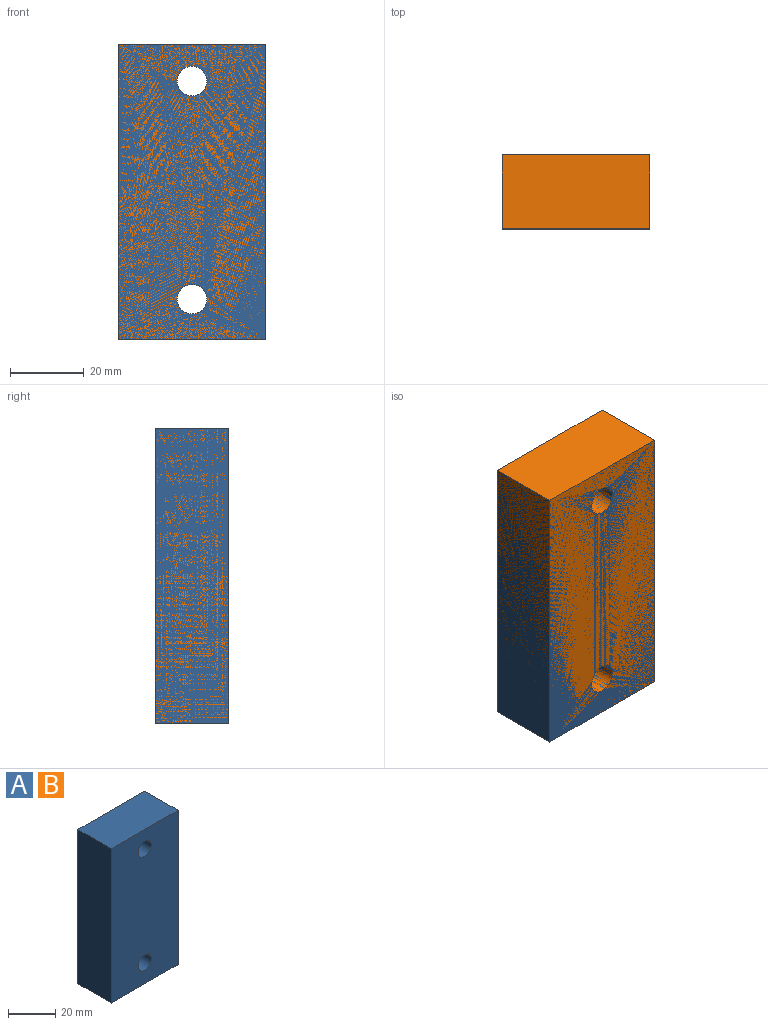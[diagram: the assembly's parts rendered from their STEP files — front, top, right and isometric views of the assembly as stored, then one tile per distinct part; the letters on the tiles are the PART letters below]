
ASSEMBLY  parts=2 mates=1
PART A: 8 faces, bbox 40x20x80 mm
  f0: plane 80x40mm, normal (0,-1,0), area 3099.5mm2, adj f1,f3,f4,f5,f6,f7
  f1: plane 80x20mm, normal (1,0,0), area 1600mm2, adj f0,f2,f4,f5
  f2: plane 80x40mm, normal (0,1,0), area 3099.5mm2, adj f1,f3,f4,f5,f6,f7
  f3: plane 80x20mm, normal (-1,0,0), area 1600mm2, adj f0,f2,f4,f5
  f4: plane 40x20mm, normal (0,0,1), area 800mm2, adj f0,f1,f2,f3
  f5: plane 40x20mm, normal (0,0,-1), area 800mm2, adj f0,f1,f2,f3
  f6: cylinder r=4mm len=20mm, axis (0,-1,0), area 502.7mm2, adj f0,f2
  f7: cylinder r=4mm len=20mm, axis (0,-1,0), area 502.7mm2, adj f0,f2
PART B: same geometry as A
PLACE A t=(-6.39,-55.14,-11.5)mm
PLACE B t=(-6.39,-55.14,-11.5)mm
MATE revolute B.f6 <-> A.f6  axis (0,-1,0) through (-6.39,-65.14,58.5)mm
